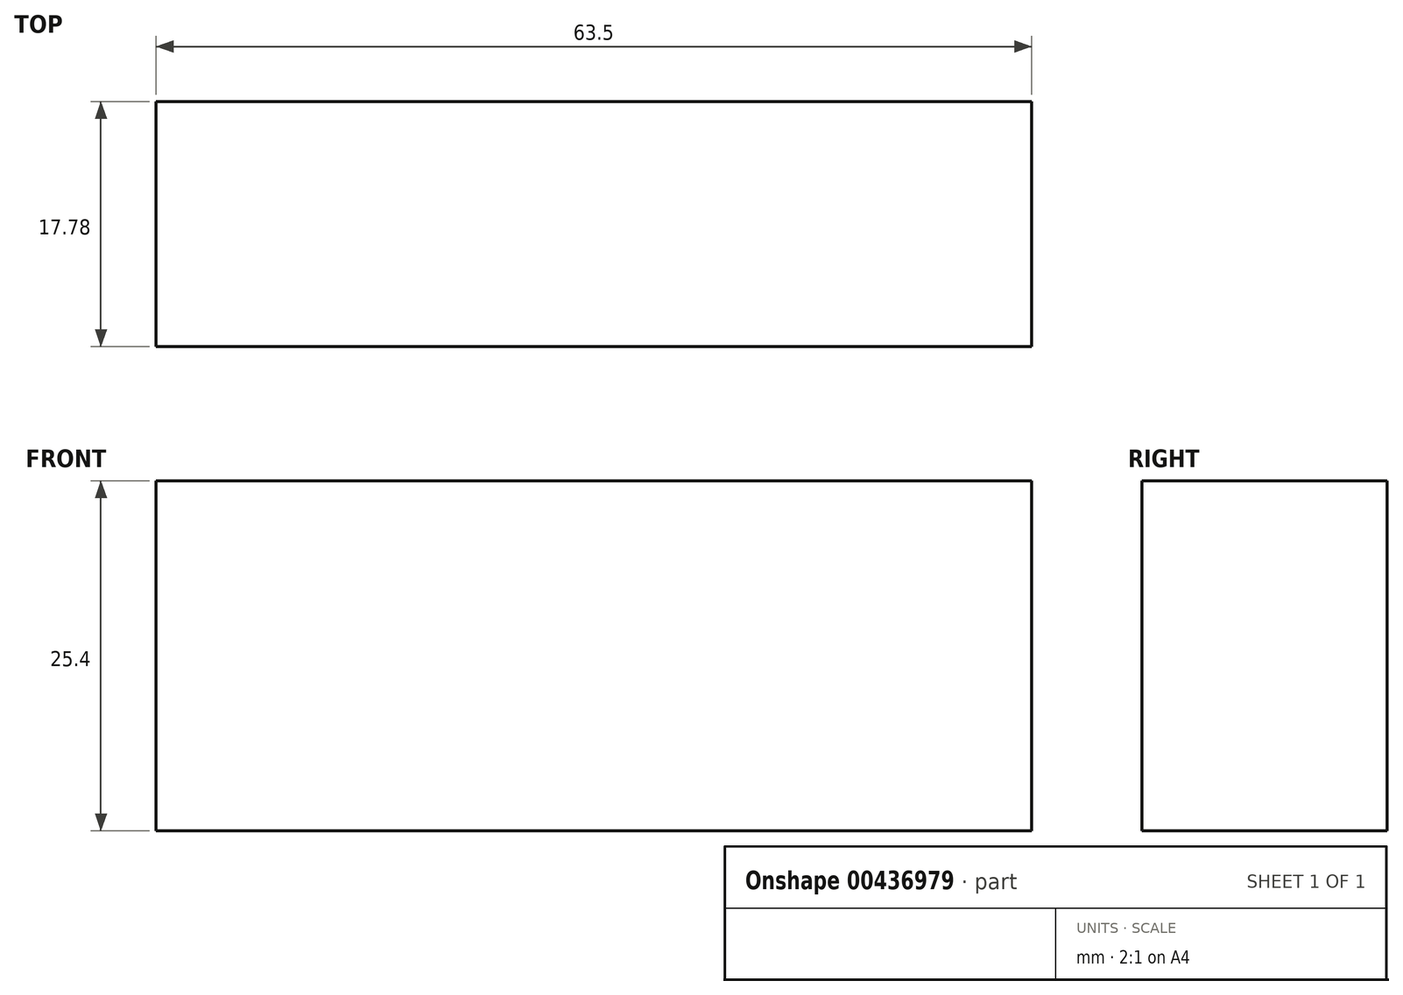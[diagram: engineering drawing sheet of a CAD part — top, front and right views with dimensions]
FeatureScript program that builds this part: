
annotation { "Feature Type Name" : "Feature", "Feature Type Description" : "" }
export const myFeature = defineFeature(function(context is Context, id is Id, definition is map)
    precondition{}
    {
        {
            var Q0;
            Q0=qCreatedBy(makeId("Front.planeOp"),FACE);
            var sketch = newSketch(context, id + "F0", { "sketchPlane" : qUnion([Q0])});
            skLineSegment(sketch, "E0.bottom", {"start": v(-43.64, 18.51) * mm, "end": v(19.86, 18.51) * mm});
            skLineSegment(sketch, "E0.top", {"start": v(-43.64, -6.89) * mm, "end": v(19.86, -6.89) * mm});
            skLineSegment(sketch, "E0.left", {"start": v(-43.64, 18.51) * mm, "end": v(-43.64, -6.89) * mm});
            skLineSegment(sketch, "E0.right", {"start": v(19.86, 18.51) * mm, "end": v(19.86, -6.89) * mm});
            skSolve(sketch);
        }
        {
            var Q0;
            Q0 = qSketchRegion(id + "F0", true);
            extrude(context, id + "F1", {"entities" : qUnion([Q0]), "depth" : 17.78 * mm});
        }
    });
